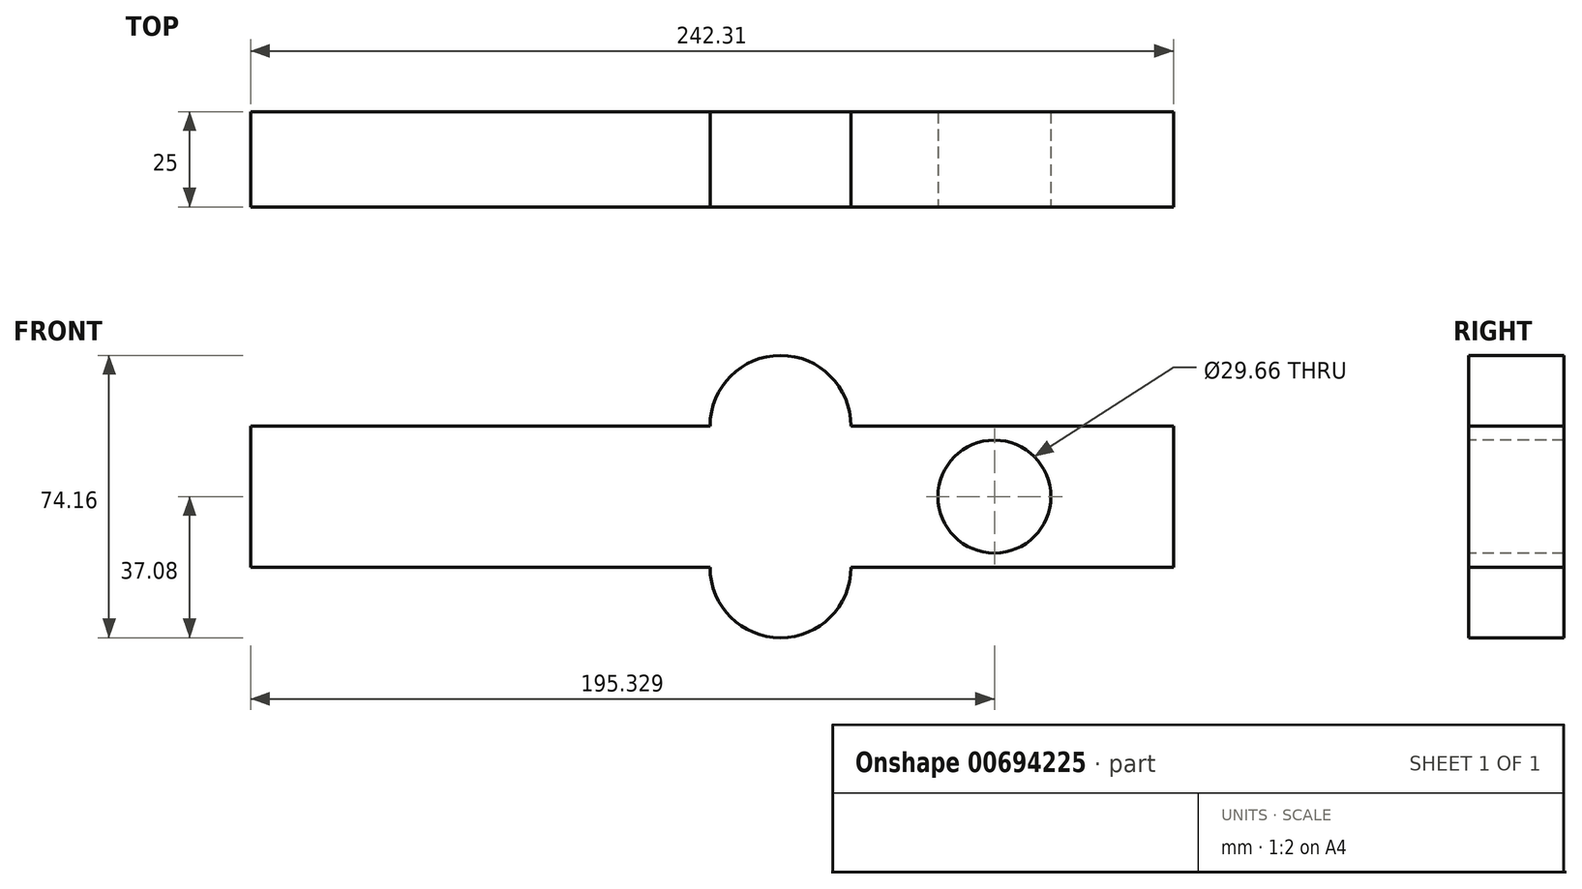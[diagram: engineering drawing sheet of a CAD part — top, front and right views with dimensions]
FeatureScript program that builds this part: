
annotation { "Feature Type Name" : "Feature", "Feature Type Description" : "" }
export const myFeature = defineFeature(function(context is Context, id is Id, definition is map)
    precondition{}
    {
        {
            var Q0;
            Q0=qCreatedBy(makeId("Front.planeOp"),FACE);
            var sketch = newSketch(context, id + "F0", { "sketchPlane" : qUnion([Q0])});
            skLineSegment(sketch, "E0.bottom", {"start": v(60.33, -18.59) * mm, "end": v(-60.33, -18.59) * mm});
            skLineSegment(sketch, "E0.top", {"start": v(60.33, 18.59) * mm, "end": v(-60.33, 18.59) * mm});
            skLineSegment(sketch, "E0.left", {"start": v(60.33, -18.59) * mm, "end": v(60.33, 18.59) * mm});
            skLineSegment(sketch, "E0.right", {"start": v(-60.33, -18.59) * mm, "end": v(-60.33, 18.59) * mm});
            skPoint(sketch, "E0.middle", {"position": v(0, 0) * mm});
            skLineSegment(sketch, "E1.bottom", {"start": v(181.98, -18.59) * mm, "end": v(97.32, -18.59) * mm});
            skLineSegment(sketch, "E1.top", {"start": v(181.98, 18.59) * mm, "end": v(97.32, 18.59) * mm});
            skLineSegment(sketch, "E1.left", {"start": v(181.98, -18.59) * mm, "end": v(181.98, 18.59) * mm});
            skLineSegment(sketch, "E1.right", {"start": v(97.32, -18.59) * mm, "end": v(97.32, 18.59) * mm});
            skPoint(sketch, "E1.middle", {"position": v(139.65, 0) * mm});
            skArc(sketch, "E2", {"start": v(60.33, 18.59) * mm, "mid": v(78.83, 37.08) * mm, "end": v(97.32, 18.59) * mm});
            skArc(sketch, "E3", {"start": v(97.32, -18.59) * mm, "mid": v(78.83, -37.08) * mm, "end": v(60.33, -18.59) * mm});
            skSolve(sketch);
        }
        {
            var Q0;
            Q0 = qSketchRegion(id + "F0", true);
            extrude(context, id + "F1", {"entities" : qUnion([Q0]), "depth" : 25 * mm, "offsetDistance" : 25 * mm});
        }
        {
            var Q0;
            Q0=makeQuery(id+"F1.opExtrude","CAP_FACE",FACE,{"disambiguationData":[OSD([sQuery(id+"F0.wireOp",EDGE,"E0.bottom"),sQuery(id+"F0.wireOp",EDGE,"E0.top"),sQuery(id+"F0.wireOp",EDGE,"E0.right"),sQuery(id+"F0.wireOp",EDGE,"E1.bottom"),sQuery(id+"F0.wireOp",EDGE,"E1.top"),sQuery(id+"F0.wireOp",EDGE,"E1.left"),sQuery(id+"F0.wireOp",EDGE,"E2"),sQuery(id+"F0.wireOp",EDGE,"E3")])],"isStart":false});
            var sketch = newSketch(context, id + "F2", { "sketchPlane" : qUnion([Q0])});
            skCircle(sketch, "E4", {"center": v(135, 0) * mm, "radius": 14.83 * mm});
            skSolve(sketch);
        }
        {
            var Q0;
            Q0 = qSketchRegion(id + "F2", true);
            extrude(context, id + "F3", {"entities" : qUnion([Q0]), "operationType" : NewBodyOperationType.REMOVE, "endBound" : BoundingType.SYMMETRIC, "oppositeDirection" : true, "depth" : 260 * mm, "offsetDistance" : 25 * mm});
        }
    });
